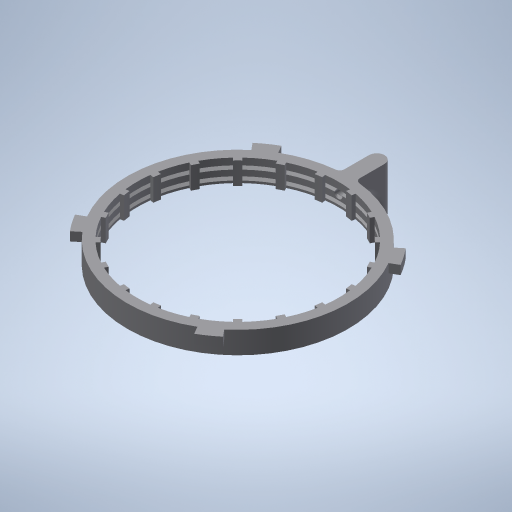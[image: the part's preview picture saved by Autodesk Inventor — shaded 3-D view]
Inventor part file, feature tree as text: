
AUTODESK INVENTOR PART (.ipt)
format: ipt  version: 2023.2 (Build 272271000, 271)  size: 694,784 bytes
history: native  units: mm
features: sketch x12, extrude x8, plane x3, hole x3, chamfer x2, pattern_circular x2, projected_geometry x2, revolve x1, sweep x1, fillet x1, mirror x1
ambient origin geometry x8: Origin, YZ Plane, XZ Plane, XY Plane, X Axis, Y Axis, Z Axis, Center Point
bodies: Solid1 (feature_tree)
feature tree (36):
  revolve  "Revolution1"  [1 undecoded]
  plane  "Work Plane2"
  sketch  "Sketch4"  dims[d18=16.75mm d21=1.5mm d22=2.0mm d23=0.289938mm]
  extrude  "Extrusion2"  Depth=2.0mm TaperAngle=0.0deg
  sweep  "Sweep1"
  hole  "Hole1"  [1 undecoded]
  extrude  "Extrusion4"  Depth=5.0mm TaperAngle=0.0deg
  fillet  "Fillet1"  [1 undecoded]
  chamfer  "Chamfer1"  Distance=0.5mm Angle=45.0deg
  sketch  "Sketch9"  dims[d46=1.0mm d47=2.0mm]
  extrude  "Extrusion5"  Depth=3.5mm
  extrude  "Extrusion6"  Depth=6.0mm
  hole  "Hole3"  [1 undecoded]
  extrude  "Extrusion8"  Depth=0.468246mm
  pattern_circular  "Circular Pattern1"  [2 undecoded]
  pattern_circular  "Circular Pattern2"  Angle=45.0deg  [1 undecoded]
  extrude  "Extrusion7"  [1 undecoded]
  mirror  "Mirror1"
  plane  "Work Plane3"
  extrude  "Extrusion3"  Depth=22.0mm
  chamfer  "Chamfer2"  Distance=1.0mm
  hole  "Hole2"  [1 undecoded]
  extrude  "Extrusion1"  Depth=22.0mm
  sketch  "Sketch1"  dims[d0=360.0deg d3=21.5mm]
  sketch  "Sketch2"  dims[d4=0.8mm d13=2.0mm d14=0.0mm]
  plane  "Work Plane1"
  sketch  "Sketch3"  dims[d15=25.0mm d17=20.5mm]
  projected_geometry  "Projected Loop1"
  projected_geometry  "Projected Loop2"
  sketch  "Sketch5"  dims[d24=5.0mm]
  sketch  "Sketch6"  dims[d25=1.8mm d26=6.0mm d27=4.3mm d28=0.5mm d29=90.0deg d30=20.0mm d31=0.0mm d33=1.0mm d34=5.0mm d35=0.0mm d36=0.0mm d37=-0.5mm d38=0.5mm d39=2.0mm d40=45.0deg]
  sketch  "Sketch7"  dims[d41=0.0mm d42=0.0mm d43=3.5mm]
  sketch  "Sketch8"  dims[d44=1.8mm d45=6.0mm]
  sketch  "Sketch10"  dims[d48=1.0mm d50=0.468246mm]
  sketch  "Sketch11"  dims[d51=41.936492mm]
  sketch  "Sketch12"  dims[d52=1.5mm d53=0.0mm d54=0.5mm d55=2.0mm d56=45.0deg d57=-2.789938mm d58=41.5mm d59=6.0mm d60=4.0mm d61=2.0mm d62=90.0deg d63=-4.0mm d64=0.0mm d70=22.0mm d72=1.0mm d75=10.0mm d76=0.0mm d77=8.0mm d78=3.0mm d80=3.2mm d81=0.0mm d82=40.0mm d83=360.0deg d85=4.5mm d86=6.0mm d87=4.0mm d88=2.0mm d89=90.0deg d90=0.1mm d91=20.594885mm d92=2.0mm d93=0.0mm d94=27.0mm d95=1.745329mm d96=30.0deg d97=43.0mm d98=48.0mm d99=0.5mm d100=0.0mm d101=2.5mm d102=22.8mm d104=13.962634mm d106=0.5mm d107=13.962634mm d110=1.5mm d114=4.5mm d115=0.0mm d116=200.0mm d117=360.0deg d119=45.0deg d120=22.0mm d121=0.5mm d122=0.5mm d123=0.5mm d124=45.0deg d125=0.8mm d71=0.872665mm d73=0.872665mm]
note: 9 required parameter values undecoded (feature->parameter linkage not recoverable at this tier; creation-order binding heuristic only, values carry confidence <= 0.55)